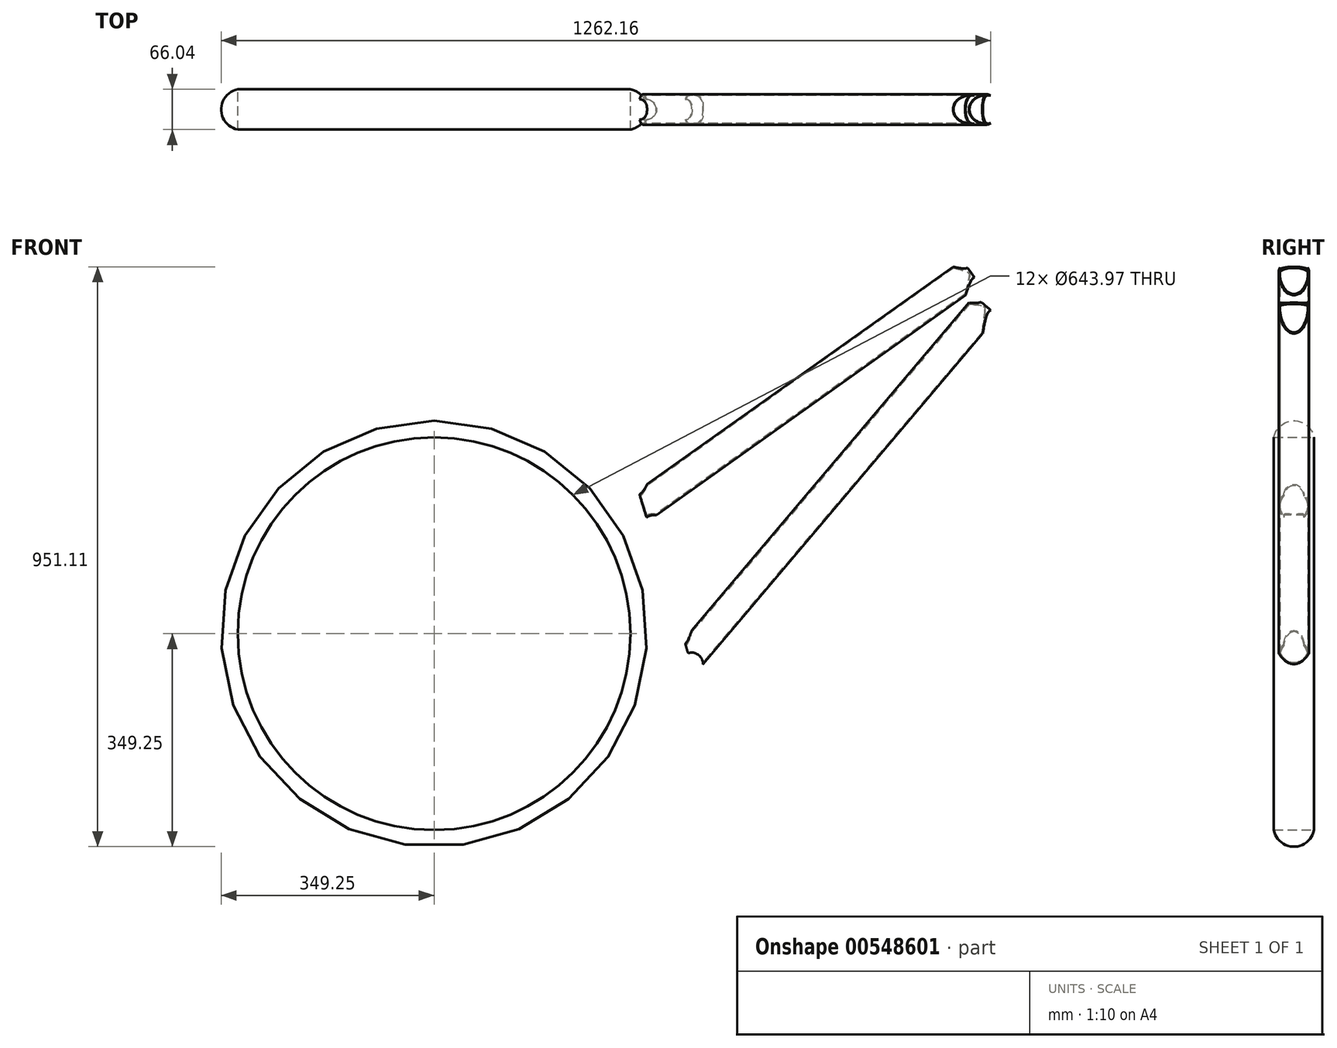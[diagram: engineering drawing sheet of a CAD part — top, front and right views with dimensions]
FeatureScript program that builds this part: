
annotation { "Feature Type Name" : "Feature", "Feature Type Description" : "" }
export const myFeature = defineFeature(function(context is Context, id is Id, definition is map)
    precondition{}
    {
        {
            var Q0;
            Q0=qCreatedBy(makeId("Front.planeOp"),FACE);
            var sketch = newSketch(context, id + "F0", { "sketchPlane" : qUnion([Q0])});
            skCircle(sketch, "E0", {"center": v(0, 349.25) * mm, "radius": 349.25 * mm});
            skLineSegment(sketch, "E1", {"start": v(0, 0) * mm, "end": v(1191.56, 0) * mm});
            skCircle(sketch, "E2", {"center": v(1191.56, 368.3) * mm, "radius": 368.3 * mm});
            skLineSegment(sketch, "E3", {"start": v(0, 349.25) * mm, "end": v(422.05, 299.25) * mm});
            skLineSegment(sketch, "E4", {"start": v(920.86, 850.92) * mm, "end": v(872.05, 960.55) * mm});
            skLineSegment(sketch, "E5", {"start": v(288.43, 736.28) * mm, "end": v(422.05, 299.25) * mm});
            skLineSegment(sketch, "E6", {"start": v(0, 349.25) * mm, "end": v(334.97, 584.06) * mm});
            skLineSegment(sketch, "E7", {"start": v(334.97, 584.06) * mm, "end": v(872.05, 960.55) * mm});
            skLineSegment(sketch, "E8", {"start": v(422.05, 299.25) * mm, "end": v(920.86, 850.92) * mm});
            skLineSegment(sketch, "E9", {"start": v(920.86, 850.92) * mm, "end": v(1144.97, 347.56) * mm});
            skLineSegment(sketch, "E10", {"start": v(1144.97, 347.56) * mm, "end": v(1191.56, 368.3) * mm});
            skSolve(sketch);
        }
        {
            var Q0;
            Q0=qCreatedBy(makeId("Front.planeOp"),FACE);
            var sketch = newSketch(context, id + "F1", { "sketchPlane" : qUnion([Q0])});
            skCircle(sketch, "E11", {"center": v(422.05, 299.25) * mm, "radius": 19.05 * mm});
            skCircle(sketch, "E12", {"center": v(422.05, 299.25) * mm, "radius": 17.4 * mm});
            skSolve(sketch);
        }
        {
            var Q0;
            Q0 = qSketchRegion(id + "F1", true);
            extrude(context, id + "F2", {"entities" : qUnion([Q0]), "endBound" : BoundingType.SYMMETRIC, "depth" : 75 * mm, "offsetDistance" : 25.4 * mm});
        }
        {
            var Q0;
            Q0=sQuery(id+"F0.wireOp",VERTEX,"E8.start");
            var Q1;
            Q1=sQuery(id+"F0.wireOp",EDGE,"E5");
            cPlane(context, id + "F3", {"entities" : qUnion([Q0, Q1]), "cplaneType" : CPlaneType.LINE_POINT, "offset" : 25 * mm, "width" : 150 * mm, "height" : 150 * mm});
        }
        {
            var Q0;
            Q0=qCreatedBy(id+"F3.planeOp",FACE);
            var sketch = newSketch(context, id + "F4", { "sketchPlane" : qUnion([Q0])});
            skCircle(sketch, "E13", {"center": v(491.1, 0) * mm, "radius": 15.55 * mm});
            skCircle(sketch, "E14", {"center": v(491.1, 0) * mm, "radius": 16.75 * mm});
            skSolve(sketch);
        }
        {
            var Q0;
            Q0=makeQuery(id+"F4.imprint","IMPRINT",FACE,{"disambiguationData":[TD([[makeQuery(id+"F4.imprint","IMPRINT",EDGE,{"derivedFrom":sQuery(id+"F4.wireOp",EDGE,"E13")}),-1.0]])]});
            extrude(context, id + "F5", {"entities" : qUnion([Q0]), "oppositeDirection" : true, "depth" : 457 * mm, "offsetDistance" : 25 * mm});
        }
        {
            var Q0;
            Q0=sQuery(id+"F0.wireOp",VERTEX,"E4.start");
            var Q1;
            Q1=sQuery(id+"F0.wireOp",EDGE,"E4");
            cPlane(context, id + "F6", {"entities" : qUnion([Q0, Q1]), "cplaneType" : CPlaneType.LINE_POINT, "offset" : 25 * mm, "width" : 150 * mm, "height" : 150 * mm});
        }
        {
            var Q0;
            Q0=qCreatedBy(id+"F6.planeOp",FACE);
            var sketch = newSketch(context, id + "F7", { "sketchPlane" : qUnion([Q0])});
            skCircle(sketch, "E15", {"center": v(1187.35, 0) * mm, "radius": 23.2 * mm});
            skCircle(sketch, "E16", {"center": v(1187.35, 0) * mm, "radius": 22 * mm});
            skSolve(sketch);
        }
        {
            var Q0;
            Q0 = qSketchRegion(id + "F7", true);
            extrude(context, id + "F8", {"entities" : qUnion([Q0]), "depth" : 120 * mm, "offsetDistance" : 25 * mm});
        }
        {
            var Q0;
            Q0=qCreatedBy(makeId("Front.planeOp"),FACE);
            var sketch = newSketch(context, id + "F9", { "sketchPlane" : qUnion([Q0])});
            skLineSegment(sketch, "E17", {"start": v(418.4, 311.2) * mm, "end": v(905, 886.52) * mm});
            skLineSegment(sketch, "E18", {"start": v(920.86, 850.92) * mm, "end": v(899.66, 841.48) * mm});
            skLineSegment(sketch, "E19", {"start": v(899.66, 841.48) * mm, "end": v(880.57, 857.63) * mm});
            skSolve(sketch);
        }
        {
            var Q0;
            Q0=sQuery(id+"F9.wireOp",EDGE,"E17");
            var Q1;
            Q1=sQuery(id+"F9.wireOp",VERTEX,"E17.end");
            cPlane(context, id + "F10", {"entities" : qUnion([Q0, Q1]), "cplaneType" : CPlaneType.LINE_POINT, "offset" : 25 * mm, "width" : 150 * mm, "height" : 150 * mm});
        }
        {
            var Q0;
            Q0=qCreatedBy(id+"F10.planeOp",FACE);
            var sketch = newSketch(context, id + "F11", { "sketchPlane" : qUnion([Q0])});
            skCircle(sketch, "E20", {"center": v(118.47, 0) * mm, "radius": 25 * mm});
            skCircle(sketch, "E21", {"center": v(118.47, 0) * mm, "radius": 23 * mm});
            skSolve(sketch);
        }
        {
            var Q0;
            Q0=makeQuery(id+"F11.imprint","IMPRINT",FACE,{"disambiguationData":[TD([[makeQuery(id+"F11.imprint","IMPRINT",EDGE,{"derivedFrom":sQuery(id+"F11.wireOp",EDGE,"E20")}),1.0]])]});
            var Q1;
            Q1=sQuery(id+"F9.wireOp",EDGE,"E17");
            sweep(context, id + "F12", {"profiles" : qUnion([Q0]), "path" : qUnion([Q1])});
        }
        {
            var Q0;
            Q0=qCreatedBy(makeId("Front.planeOp"),FACE);
            var sketch = newSketch(context, id + "F13", { "sketchPlane" : qUnion([Q0])});
            skLineSegment(sketch, "E22", {"start": v(880.51, 941.53) * mm, "end": v(335.89, 554.03) * mm});
            skLineSegment(sketch, "E23", {"start": v(349.47, 563.7) * mm, "end": v(334.97, 584.06) * mm});
            skLineSegment(sketch, "E24", {"start": v(335.89, 554.03) * mm, "end": v(350.38, 533.66) * mm});
            skLineSegment(sketch, "E25", {"start": v(865.35, 930.74) * mm, "end": v(850.85, 951.1) * mm});
            skLineSegment(sketch, "E26", {"start": v(872.05, 960.55) * mm, "end": v(850.85, 951.1) * mm});
            skSolve(sketch);
        }
        {
            var Q0;
            Q0=sQuery(id+"F13.wireOp",EDGE,"E22");
            var Q1;
            Q1=sQuery(id+"F13.wireOp",VERTEX,"E22.start");
            cPlane(context, id + "F14", {"entities" : qUnion([Q0, Q1]), "cplaneType" : CPlaneType.LINE_POINT, "offset" : 25 * mm, "width" : 150 * mm, "height" : 150 * mm});
        }
        {
            var Q0;
            Q0=qCreatedBy(id+"F14.planeOp",FACE);
            var sketch = newSketch(context, id + "F15", { "sketchPlane" : qUnion([Q0])});
            skCircle(sketch, "E27", {"center": v(0, 256.7) * mm, "radius": 25 * mm});
            skCircle(sketch, "E28", {"center": v(0, 256.7) * mm, "radius": 23 * mm});
            skSolve(sketch);
        }
        {
            var Q0;
            Q0=makeQuery(id+"F15.imprint","IMPRINT",FACE,{"disambiguationData":[TD([[makeQuery(id+"F15.imprint","IMPRINT",EDGE,{"derivedFrom":sQuery(id+"F15.wireOp",EDGE,"E27")}),1.0]])]});
            var Q1;
            Q1=sQuery(id+"F13.wireOp",EDGE,"E22");
            sweep(context, id + "F16", {"profiles" : qUnion([Q0]), "path" : qUnion([Q1])});
        }
        {
            var Q0;
            Q0=makeQuery(id+"F7.imprint","IMPRINT",FACE,{"disambiguationData":[TD([[makeQuery(id+"F7.imprint","IMPRINT",EDGE,{"derivedFrom":sQuery(id+"F7.wireOp",EDGE,"E16")}),1.0]])]});
            var Q1;
            Q1=makeQuery(id+"F7.imprint","IMPRINT",FACE,{"disambiguationData":[TD([[makeQuery(id+"F7.imprint","IMPRINT",EDGE,{"derivedFrom":sQuery(id+"F7.wireOp",EDGE,"E15")}),1.0]])]});
            extrude(context, id + "F17", {"entities" : qUnion([Q0, Q1]), "operationType" : NewBodyOperationType.REMOVE, "endBound" : BoundingType.THROUGH_ALL, "depth" : 25 * mm, "offsetDistance" : 25 * mm, "hasSecondDirection" : true, "secondDirectionBound" : SecondDirectionBoundingType.THROUGH_ALL, "secondDirectionOppositeDirection" : true, "secondDirectionDepth" : 25 * mm});
        }
        {
            var Q0;
            Q0=makeQuery(id+"F2.opExtrude","CAP_FACE",FACE,{"disambiguationData":[OSD([sQuery(id+"F1.wireOp",EDGE,"E11"),sQuery(id+"F1.wireOp",EDGE,"E12")])],"isStart":false});
            var Q1;
            Q1=makeQuery(id+"F1.imprint","IMPRINT",FACE,{"disambiguationData":[TD([[makeQuery(id+"F1.imprint","IMPRINT",EDGE,{"derivedFrom":sQuery(id+"F1.wireOp",EDGE,"E12")}),1.0]])]});
            extrude(context, id + "F18", {"entities" : qUnion([Q0, Q1]), "operationType" : NewBodyOperationType.REMOVE, "endBound" : BoundingType.THROUGH_ALL, "oppositeDirection" : true, "depth" : 25.4 * mm, "offsetDistance" : 25.4 * mm, "hasSecondDirection" : true, "secondDirectionBound" : SecondDirectionBoundingType.THROUGH_ALL, "secondDirectionOppositeDirection" : false, "secondDirectionDepth" : 25.4 * mm});
        }
        {
            var Q0;
            Q0=qCreatedBy(id+"F3.planeOp",FACE);
            var sketch = newSketch(context, id + "F19", { "sketchPlane" : qUnion([Q0])});
            skArc(sketch, "E29", {"start": v(491.1, -16.75) * mm, "mid": v(507.85, 0) * mm, "end": v(491.1, 16.75) * mm});
            skLineSegment(sketch, "E30", {"start": v(491.1, 16.75) * mm, "end": v(491.1, 42.05) * mm});
            skLineSegment(sketch, "E31", {"start": v(491.1, 42.05) * mm, "end": v(464.84, 42.05) * mm});
            skLineSegment(sketch, "E32", {"start": v(464.84, 42.05) * mm, "end": v(464.84, -46.57) * mm});
            skLineSegment(sketch, "E33", {"start": v(464.84, -46.57) * mm, "end": v(491.1, -46.57) * mm});
            skLineSegment(sketch, "E34", {"start": v(491.1, -46.57) * mm, "end": v(491.1, -16.75) * mm});
            skSolve(sketch);
        }
        {
            var Q0;
            Q0 = qSketchRegion(id + "F19", true);
            extrude(context, id + "F20", {"entities" : qUnion([Q0]), "operationType" : NewBodyOperationType.REMOVE, "endBound" : BoundingType.THROUGH_ALL, "oppositeDirection" : true, "depth" : 25 * mm, "offsetDistance" : 25 * mm});
        }
        {
            var Q0;
            Q0=qCreatedBy(makeId("Right.planeOp"),FACE);
            var sketch = newSketch(context, id + "F21", { "sketchPlane" : qUnion([Q0])});
            skArc(sketch, "E35", {"start": v(-33.02, 27.27) * mm, "mid": v(0, 0) * mm, "end": v(33.02, 27.27) * mm});
            skLineSegment(sketch, "E36", {"start": v(33.02, 27.27) * mm, "end": v(-33.02, 27.27) * mm});
            skSolve(sketch);
        }
        {
            var Q0;
            Q0=makeQuery(id+"F21.imprint","IMPRINT",FACE,{"disambiguationData":[TD([[makeQuery(id+"F21.imprint","IMPRINT",EDGE,{"derivedFrom":sQuery(id+"F21.wireOp",EDGE,"E35")}),1.0]])]});
            var Q1;
            Q1=sQuery(id+"F0.wireOp",EDGE,"E0");
            revolve(context, id + "F22", {"entities" : qUnion([Q0]), "axis" : qUnion([Q1]), "revolveType" : RevolveType.FULL});
        }
    });
